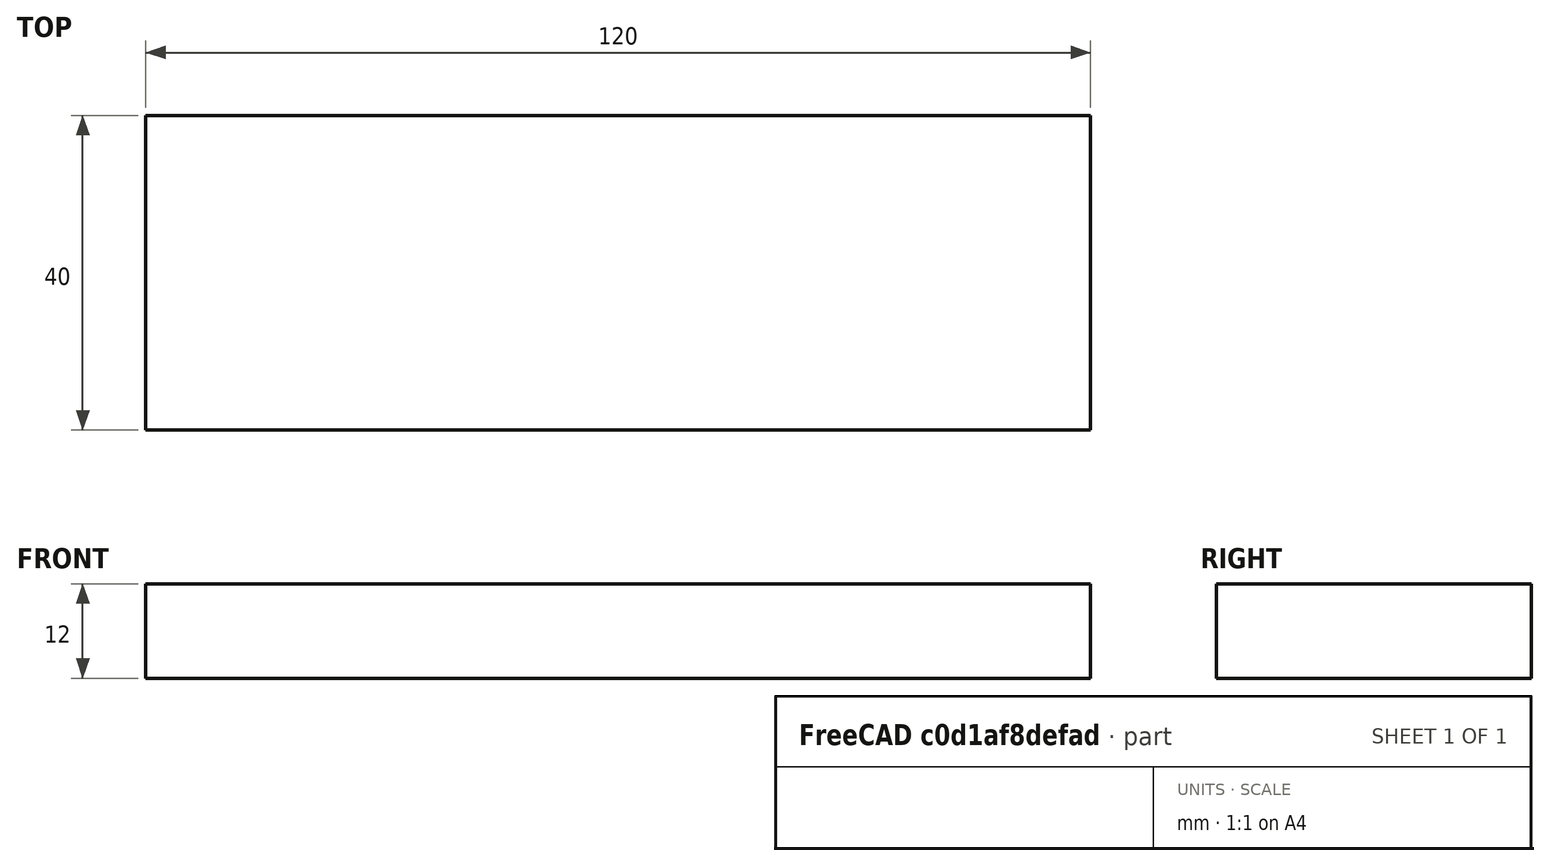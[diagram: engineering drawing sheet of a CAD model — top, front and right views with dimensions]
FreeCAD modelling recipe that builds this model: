
FCSTD DOCUMENT  (FreeCAD 0.15R4671 (Git))
Label: Tisch X-Achse - Top
License: All rights reserved
LicenseURL: http://de.wikipedia.org/wiki/Alle_Rechte_vorbehalten
objects: Sketcher::SketchObject×1, PartDesign::Pad×1
note: 3 computed .brp shape members not serialized (recipe doc carries the construction recipe); baked Part::Feature solids carry a one-line shape summary decoded from their .brp

FEATURE [Sketcher::SketchObject] Sketch
  sketch-geometry (4):
    g0: LineSegment StartX=-60 StartY=20 StartZ=0 EndX=60 EndY=20 EndZ=0
    g1: LineSegment StartX=60 StartY=20 StartZ=0 EndX=60 EndY=-20 EndZ=0
    g2: LineSegment StartX=60 StartY=-20 StartZ=0 EndX=-60 EndY=-20 EndZ=0
    g3: LineSegment StartX=-60 StartY=-20 StartZ=0 EndX=-60 EndY=20 EndZ=0
  constraints (12):
    c: Coincident(g0,g1)
    c: Coincident(g1,g2)
    c: Coincident(g2,g3)
    c: Coincident(g3,g0)
    c: Horizontal(g0)
    c: Horizontal(g2)
    c: Vertical(g1)
    c: Vertical(g3)
    c: Symmetric(g1,g0,g-1)
    c: Symmetric(g0,g0,g-2)
    c: DistanceY(g1) = -40
    c: DistanceX(g0) = 120
FEATURE [PartDesign::Pad] Pad
  Length = 12
  Length2 = 100
  Sketch = -> Sketch
  Type = 0
